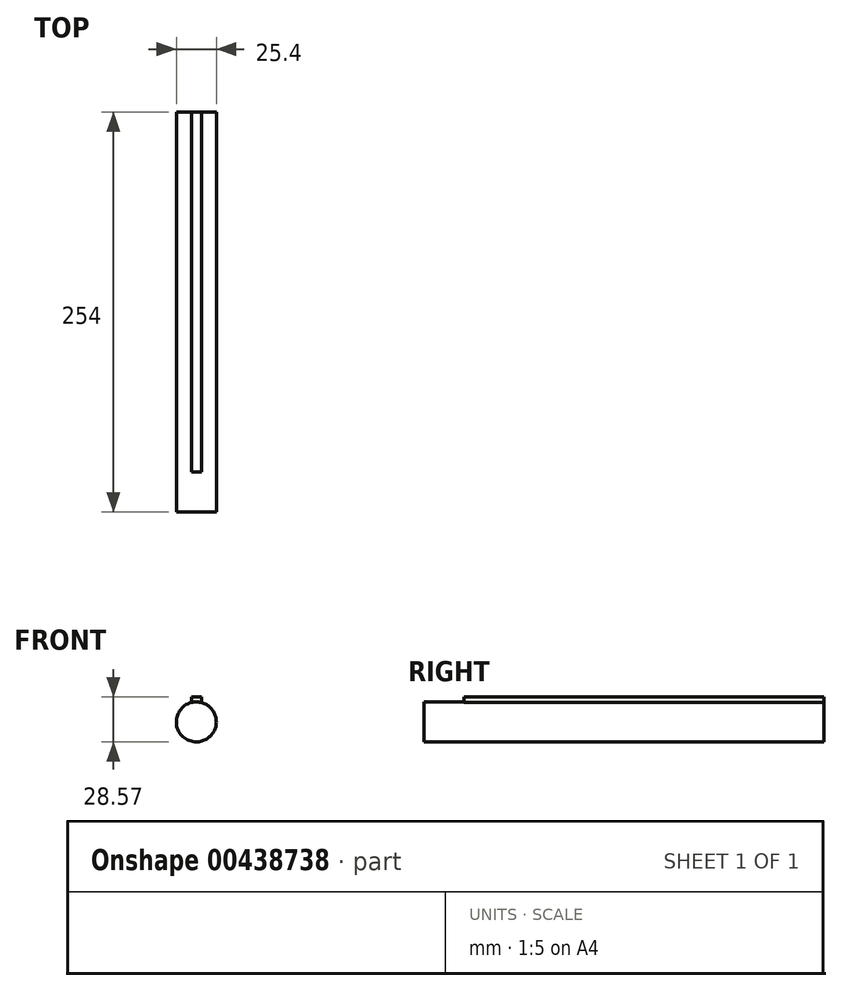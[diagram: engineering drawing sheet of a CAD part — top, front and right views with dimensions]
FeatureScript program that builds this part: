
annotation { "Feature Type Name" : "Feature", "Feature Type Description" : "" }
export const myFeature = defineFeature(function(context is Context, id is Id, definition is map)
    precondition{}
    {
        {
            var Q0;
            Q0=qCreatedBy(makeId("Front.planeOp"),FACE);
            var sketch = newSketch(context, id + "F0", { "sketchPlane" : qUnion([Q0])});
            skCircle(sketch, "E0", {"center": v(-36.69, 43.8) * mm, "radius": 12.7 * mm});
            skLineSegment(sketch, "E1", {"start": v(-36.69, 43.8) * mm, "end": v(-36.69, 59.68) * mm});
            skLineSegment(sketch, "E2", {"start": v(-36.69, 59.68) * mm, "end": v(-39.86, 59.68) * mm});
            skLineSegment(sketch, "E3", {"start": v(-39.86, 59.68) * mm, "end": v(-39.86, 56.1) * mm});
            skLineSegment(sketch, "E4.MirrorCS", {"start": v(-36.69, 59.68) * mm, "end": v(-33.51, 59.68) * mm});
            skLineSegment(sketch, "E5.MirrorCS", {"start": v(-33.51, 59.68) * mm, "end": v(-33.51, 56.1) * mm});
            skSolve(sketch);
        }
        {
            var Q0;
            {var subQ0=sQuery(id+"F0.wireOp",EDGE,"E0");var subQ1=makeQuery(id+"F0.imprint","INTERSECT",VERTEX,{"derivedFrom":[subQ0,sQuery(id+"F0.wireOp",EDGE,"E5.MirrorCS")]});Q0=makeQuery(id+"F0.imprint","IMPRINT",FACE,{"disambiguationData":[TD([[makeQuery(id+"F0.imprint","IMPRINT",EDGE,{"disambiguationData":[TD([[subQ1,-1.0]])],"derivedFrom":subQ0}),1.0]])]});}
            extrude(context, id + "F1", {"entities" : qUnion([Q0]), "depth" : 254 * mm});
        }
        {
            var Q0;
            {var subQ4=sQuery(id+"F0.wireOp",EDGE,"E2");Q0=makeQuery(id+"F0.imprint","IMPRINT",FACE,{"disambiguationData":[TD([[makeQuery(id+"F0.imprint","IMPRINT",EDGE,{"derivedFrom":subQ4}),1.0]])]});}
            var Q1;
            {var subQ4=sQuery(id+"F0.wireOp",EDGE,"E4.MirrorCS");Q1=makeQuery(id+"F0.imprint","IMPRINT",FACE,{"disambiguationData":[TD([[makeQuery(id+"F0.imprint","IMPRINT",EDGE,{"derivedFrom":subQ4}),-1.0]])]});}
            extrude(context, id + "F2", {"entities" : qUnion([Q0, Q1]), "operationType" : NewBodyOperationType.ADD, "depth" : 228.6 * mm});
        }
    });
